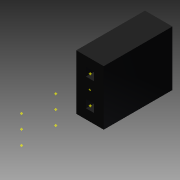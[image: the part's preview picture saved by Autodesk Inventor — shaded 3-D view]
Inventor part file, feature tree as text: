
AUTODESK INVENTOR PART (.ipt)
format: ipt  version: 2013 (Build 170138000, 138)  size: 87,040 bytes
history: native  units: in
note: dims shown in document units (in); Inventor stores cm internally (conversion verified against a paired STEP export)
features: other x12, plane x6, extrude x1, sketch x1
ambient origin geometry x8: Origin, YZ Plane, XZ Plane, XY Plane, X Axis, Y Axis, Z Axis, Center Point
bodies: Solid1 (feature_tree)
feature tree (20):
  extrude  "Extrusion1"  Depth=0.125in
  other  "Work Point8"
  other  "Work Point9"
  other  "Work Point10"
  other  "Work Point11"
  other  "Work Point13"
  other  "Work Point14"
  sketch  "Sketch1"  dims[d0=0.25in d1=0.0in d3=0.125in d4=0.25in d5=0.125in d6=0.25in d7=0.125in d8=0.25in]
  plane  "Work Plane6"
  other  "Work Axis6"
  plane  "Work Plane7"
  other  "Work Axis7"
  plane  "Work Plane8"
  other  "Work Axis8"
  plane  "Work Plane9"
  other  "Work Axis9"
  plane  "Work Plane10"
  other  "Work Axis10"
  plane  "Work Plane11"
  other  "Work Axis11"
